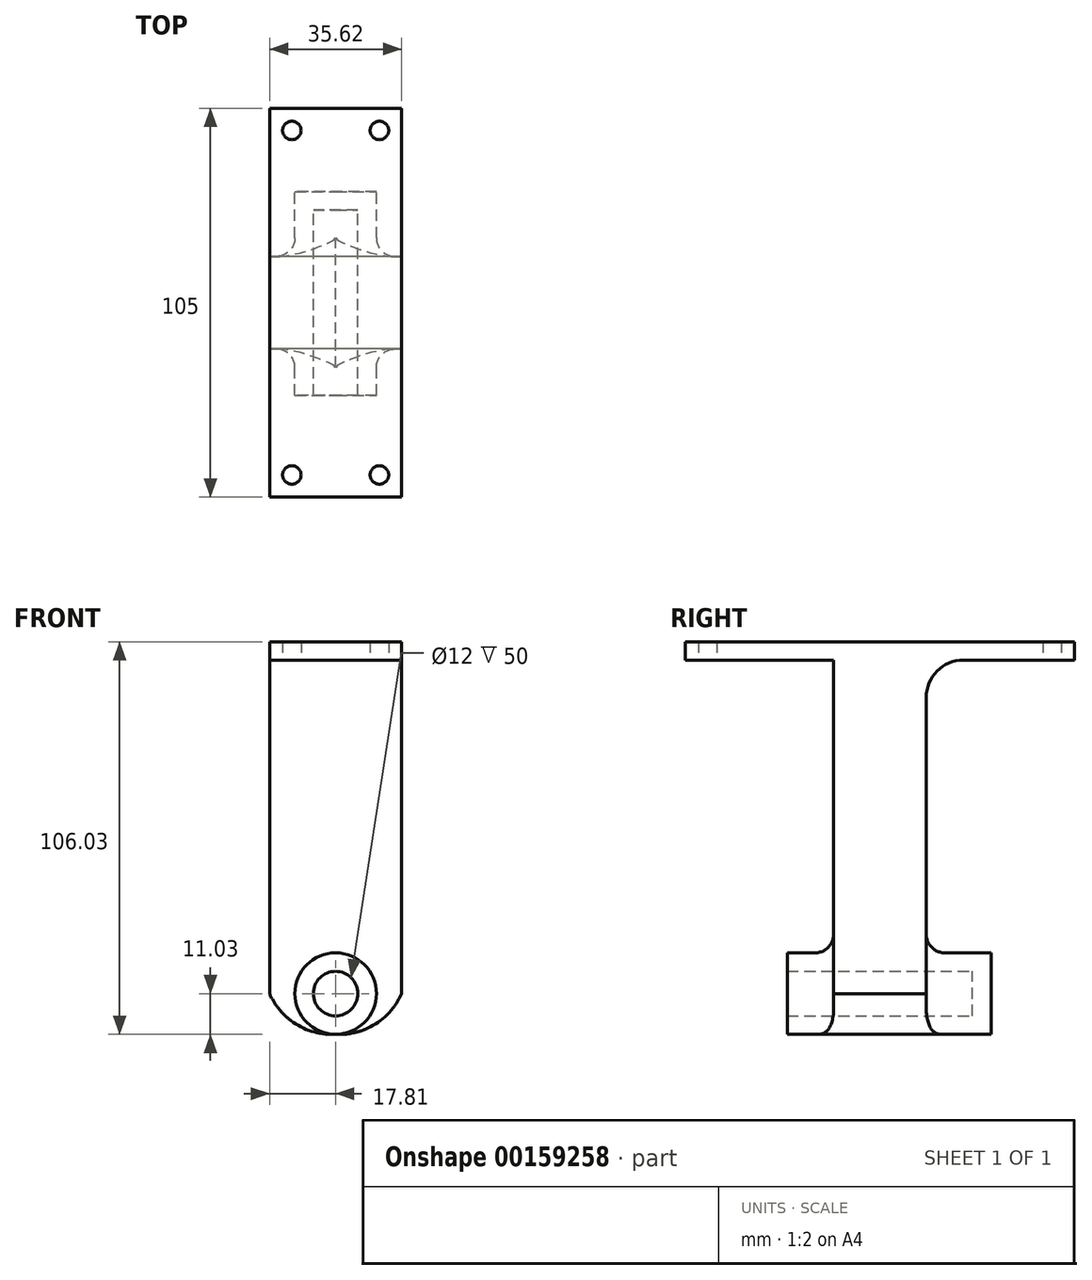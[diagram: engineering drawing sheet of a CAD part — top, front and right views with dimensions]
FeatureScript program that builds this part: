
annotation { "Feature Type Name" : "Feature", "Feature Type Description" : "" }
export const myFeature = defineFeature(function(context is Context, id is Id, definition is map)
    precondition{}
    {
        {
            var Q0;
            Q0=qCreatedBy(makeId("Front.planeOp"),FACE);
            var sketch = newSketch(context, id + "F0", { "sketchPlane" : qUnion([Q0])});
            skCircle(sketch, "E0", {"center": v(0, 0) * mm, "radius": 6 * mm});
            skCircle(sketch, "E1.0", {"center": v(0, 0) * mm, "radius": 11 * mm});
            skSolve(sketch);
        }
        {
            var Q0;
            Q0 = qSketchRegion(id + "F0", true);
            extrude(context, id + "F1", {"entities" : qUnion([Q0]), "endBound" : BoundingType.SYMMETRIC, "depth" : 50 * mm});
        }
        {
            var Q0;
            Q0=makeQuery(id+"F1.opExtrude","CAP_FACE",FACE,{"disambiguationData":[OSD([sQuery(id+"F0.wireOp",EDGE,"E0"),sQuery(id+"F0.wireOp",EDGE,"E1.0")])],"isStart":true});
            var sketch = newSketch(context, id + "F2", { "sketchPlane" : qUnion([Q0])});
            skCircle(sketch, "E2.0", {"center": v(0, 0) * mm, "radius": 11 * mm});
            skSolve(sketch);
        }
        {
            var Q0;
            Q0 = qSketchRegion(id + "F2", true);
            extrude(context, id + "F3", {"entities" : qUnion([Q0]), "operationType" : NewBodyOperationType.ADD, "depth" : 5 * mm});
        }
        {
            var Q0;
            Q0=qCreatedBy(makeId("Front.planeOp"),FACE);
            var sketch = newSketch(context, id + "F4", { "sketchPlane" : qUnion([Q0])});
            skCircle(sketch, "E3.0", {"center": v(0, 0) * mm, "radius": 11 * mm});
            skArc(sketch, "E4", {"start": v(0, -11) * mm, "mid": v(10.63, -8.29) * mm, "end": v(17.81, 0) * mm});
            skArc(sketch, "E5.MirrorCS", {"start": v(0, -11) * mm, "mid": v(-10.63, -8.29) * mm, "end": v(-17.81, 0) * mm});
            skLineSegment(sketch, "E6", {"start": v(-17.81, 0) * mm, "end": v(-17.81, 90) * mm});
            skLineSegment(sketch, "E7", {"start": v(17.81, 0) * mm, "end": v(17.81, 90) * mm});
            skLineSegment(sketch, "E8", {"start": v(17.81, 90) * mm, "end": v(-17.81, 90) * mm});
            skSolve(sketch);
        }
        {
            var Q0;
            Q0 = qSketchRegion(id + "F4", true);
            extrude(context, id + "F5", {"entities" : qUnion([Q0]), "operationType" : NewBodyOperationType.ADD, "endBound" : BoundingType.SYMMETRIC, "depth" : 25 * mm});
        }
        {
            var Q0;
            Q0=makeQuery(id+"F5.opExtrude","SWEPT_FACE",FACE,{"disambiguationData":[OSD([sQuery(id+"F4.wireOp",EDGE,"E8")])]});
            var sketch = newSketch(context, id + "F6", { "sketchPlane" : qUnion([Q0])});
            skLineSegment(sketch, "E9.0", {"start": v(17.81, -12.5) * mm, "end": v(17.81, 12.5) * mm});
            skLineSegment(sketch, "E10.0", {"start": v(-17.81, -12.5) * mm, "end": v(-17.81, 12.5) * mm});
            skLineSegment(sketch, "E11", {"start": v(17.81, -12.5) * mm, "end": v(17.81, -52.5) * mm});
            skLineSegment(sketch, "E12.MirrorCS", {"start": v(17.81, 12.5) * mm, "end": v(17.81, 52.5) * mm});
            skLineSegment(sketch, "E13.MirrorCS", {"start": v(-17.81, -12.5) * mm, "end": v(-17.81, -52.5) * mm});
            skLineSegment(sketch, "E14.MirrorCS", {"start": v(-17.81, 12.5) * mm, "end": v(-17.81, 52.5) * mm});
            skLineSegment(sketch, "E15", {"start": v(17.81, 52.5) * mm, "end": v(-17.81, 52.5) * mm});
            skLineSegment(sketch, "E16", {"start": v(-17.81, -52.5) * mm, "end": v(17.81, -52.5) * mm});
            skSolve(sketch);
        }
        {
            var Q0;
            Q0 = qSketchRegion(id + "F6", true);
            extrude(context, id + "F7", {"entities" : qUnion([Q0]), "operationType" : NewBodyOperationType.ADD, "depth" : 5 * mm});
        }
        {
            var Q0;
            Q0=makeQuery(id+"F5.opExtrude","CAP_EDGE",EDGE,{"disambiguationData":[OSD([sQuery(id+"F4.wireOp",EDGE,"E8")])],"isStart":false});
            var Q1;
            Q1=makeQuery(id+"F5.opExtrude","CAP_EDGE",EDGE,{"disambiguationData":[OSD([sQuery(id+"F4.wireOp",EDGE,"E8")])],"isStart":true});
            fillet(context, id + "F8", {"entities" : qUnion([Q0, Q1]), "radius" : 10 * mm, "tangentPropagation" : true, "allowEdgeOverflow" : false});
        }
        {
            var Q0;
            Q0=makeQuery(id+"F5.boolean.opBoolean","INTERSECT",EDGE,{"derivedFrom":[makeQuery(id+"F3.boolean.opBoolean","MERGE",FACE,{"derivedFrom":[makeQuery(id+"F1.opExtrude","SWEPT_FACE",FACE,{"disambiguationData":[OSD([sQuery(id+"F0.wireOp",EDGE,"E1.0")])]}),makeQuery(id+"F3.opExtrude","SWEPT_FACE",FACE,{"disambiguationData":[OSD([sQuery(id+"F2.wireOp",EDGE,"E2.0")])]})]}),makeQuery(id+"F5.opExtrude","CAP_FACE",FACE,{"disambiguationData":[OSD([sQuery(id+"F4.wireOp",EDGE,"E4"),sQuery(id+"F4.wireOp",EDGE,"E5.MirrorCS"),sQuery(id+"F4.wireOp",EDGE,"E6"),sQuery(id+"F4.wireOp",EDGE,"E7"),sQuery(id+"F4.wireOp",EDGE,"E8")])],"isStart":false})]});
            var Q1;
            Q1=makeQuery(id+"F5.boolean.opBoolean","INTERSECT",EDGE,{"derivedFrom":[makeQuery(id+"F3.boolean.opBoolean","MERGE",FACE,{"derivedFrom":[makeQuery(id+"F1.opExtrude","SWEPT_FACE",FACE,{"disambiguationData":[OSD([sQuery(id+"F0.wireOp",EDGE,"E1.0")])]}),makeQuery(id+"F3.opExtrude","SWEPT_FACE",FACE,{"disambiguationData":[OSD([sQuery(id+"F2.wireOp",EDGE,"E2.0")])]})]}),makeQuery(id+"F5.opExtrude","CAP_FACE",FACE,{"disambiguationData":[OSD([sQuery(id+"F4.wireOp",EDGE,"E4"),sQuery(id+"F4.wireOp",EDGE,"E5.MirrorCS"),sQuery(id+"F4.wireOp",EDGE,"E6"),sQuery(id+"F4.wireOp",EDGE,"E7"),sQuery(id+"F4.wireOp",EDGE,"E8")])],"isStart":true})]});
            fillet(context, id + "F9", {"entities" : qUnion([Q0, Q1]), "radius" : 5 * mm, "tangentPropagation" : true, "allowEdgeOverflow" : false});
        }
        {
            var Q0;
            Q0=makeQuery(id+"F5.boolean.opBoolean","SPLIT",FACE,{"disambiguationData":[TD([makeQuery(id+"F1.opExtrude","SWEPT_FACE",FACE,{"disambiguationData":[OSD([sQuery(id+"F0.wireOp",EDGE,"E0")])]})])],"derivedFrom":makeQuery(id+"F5.opExtrude","CAP_FACE",FACE,{"disambiguationData":[OSD([sQuery(id+"F4.wireOp",EDGE,"E4"),sQuery(id+"F4.wireOp",EDGE,"E5.MirrorCS"),sQuery(id+"F4.wireOp",EDGE,"E6"),sQuery(id+"F4.wireOp",EDGE,"E7"),sQuery(id+"F4.wireOp",EDGE,"E8")])],"isStart":false})});
            var sketch = newSketch(context, id + "F10", { "sketchPlane" : qUnion([Q0])});
            skCircle(sketch, "E17.0", {"center": v(0, 0) * mm, "radius": 6 * mm});
            skSolve(sketch);
        }
        {
            var Q0;
            Q0 = qSketchRegion(id + "F10", true);
            var Q1;
            {var subQ0=sQuery(id+"F2.wireOp",EDGE,"E2.0");Q1=makeQuery(id+"F5.boolean.opBoolean","SPLIT",FACE,{"disambiguationData":[TD([makeQuery(id+"F3.opExtrude","CAP_FACE",FACE,{"disambiguationData":[OSD([subQ0])],"isStart":false})])],"derivedFrom":makeQuery(id+"F3.boolean.opBoolean","MERGE",FACE,{"derivedFrom":[makeQuery(id+"F1.opExtrude","SWEPT_FACE",FACE,{"disambiguationData":[OSD([sQuery(id+"F0.wireOp",EDGE,"E1.0")])]}),makeQuery(id+"F3.opExtrude","SWEPT_FACE",FACE,{"disambiguationData":[OSD([subQ0])]})]})});}
            extrude(context, id + "F11", {"entities" : qUnion([Q0]), "operationType" : NewBodyOperationType.REMOVE, "oppositeDirection" : true, "endBoundEntityFace" : qUnion([Q1]), "depth" : 30 * mm});
        }
        {
            var Q0;
            {var subQ0=sQuery(id+"F6.wireOp",EDGE,"E12.MirrorCS");var subQ1=sQuery(id+"F6.wireOp",EDGE,"E11");var subQ2=sQuery(id+"F6.wireOp",EDGE,"E9.0");var subQ5=sQuery(id+"F6.wireOp",EDGE,"E14.MirrorCS");var subQ6=sQuery(id+"F6.wireOp",EDGE,"E13.MirrorCS");var subQ7=sQuery(id+"F6.wireOp",EDGE,"E10.0");var subQ8=sQuery(id+"F6.wireOp",EDGE,"E16");Q0=makeQuery(id+"F7.boolean.opBoolean","SPLIT",FACE,{"disambiguationData":[TD([makeQuery(id+"F7.opExtrude","SWEPT_FACE",FACE,{"disambiguationData":[OSD([subQ8])]})])],"derivedFrom":makeQuery(id+"F7.opExtrude","CAP_FACE",FACE,{"disambiguationData":[OSD([subQ2,subQ7,subQ1,subQ0,subQ6,subQ5,sQuery(id+"F6.wireOp",EDGE,"E15"),subQ8])],"isStart":true})});}
            var sketch = newSketch(context, id + "F12", { "sketchPlane" : qUnion([Q0])});
            skLineSegment(sketch, "E18.0", {"start": v(-17.81, 22.5) * mm, "end": v(-17.81, 52.5) * mm, "construction": true});
            skLineSegment(sketch, "E19.0", {"start": v(-17.81, 52.5) * mm, "end": v(17.81, 52.5) * mm, "construction": true});
            skLineSegment(sketch, "E20.0", {"start": v(17.81, 22.5) * mm, "end": v(17.81, 52.5) * mm, "construction": true});
            skLineSegment(sketch, "E21.0", {"start": v(17.81, -52.5) * mm, "end": v(17.81, -22.5) * mm, "construction": true});
            skLineSegment(sketch, "E22.0", {"start": v(17.81, -52.5) * mm, "end": v(-17.81, -52.5) * mm, "construction": true});
            skLineSegment(sketch, "E23.0", {"start": v(-17.81, -52.5) * mm, "end": v(-17.81, -22.5) * mm, "construction": true});
            skCircle(sketch, "E24", {"center": v(-11.81, 46.5) * mm, "radius": 2.5 * mm});
            skCircle(sketch, "E25.MirrorC", {"center": v(11.81, 46.5) * mm, "radius": 2.5 * mm});
            skCircle(sketch, "E26.MirrorC", {"center": v(-11.81, -46.5) * mm, "radius": 2.5 * mm});
            skCircle(sketch, "E27.MirrorC", {"center": v(11.81, -46.5) * mm, "radius": 2.5 * mm});
            skSolve(sketch);
        }
        {
            var Q0;
            Q0 = qSketchRegion(id + "F12", true);
            extrude(context, id + "F13", {"entities" : qUnion([Q0]), "operationType" : NewBodyOperationType.REMOVE, "endBound" : BoundingType.THROUGH_ALL, "oppositeDirection" : true, "depth" : 25 * mm});
        }
    });
